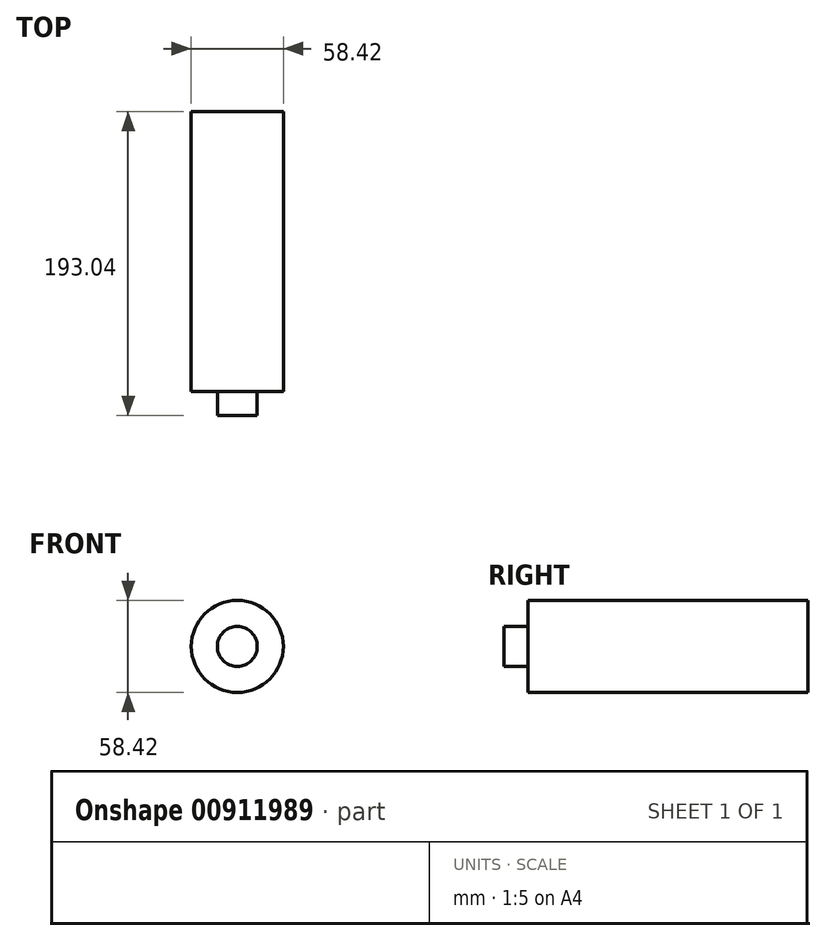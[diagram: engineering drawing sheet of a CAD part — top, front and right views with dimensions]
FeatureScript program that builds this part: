
annotation { "Feature Type Name" : "Feature", "Feature Type Description" : "" }
export const myFeature = defineFeature(function(context is Context, id is Id, definition is map)
    precondition{}
    {
        {
            var Q0;
            Q0=qCreatedBy(makeId("Front.planeOp"),FACE);
            var sketch = newSketch(context, id + "F0", { "sketchPlane" : qUnion([Q0])});
            skCircle(sketch, "E0", {"center": v(0, 0) * mm, "radius": 29.21 * mm});
            skPoint(sketch, "E1.orphan", {"position": v(0, 29.21) * mm});
            skSolve(sketch);
        }
        {
            var Q0;
            Q0=makeQuery(id+"F0.imprint","IMPRINT",FACE,{"disambiguationData":[TD([[makeQuery(id+"F0.imprint","IMPRINT",EDGE,{"derivedFrom":sQuery(id+"F0.wireOp",EDGE,"E0")}),1.0]])]});
            extrude(context, id + "F1", {"entities" : qUnion([Q0]), "depth" : 177.8 * mm, "offsetDistance" : 25.4 * mm});
        }
        {
            var Q0;
            Q0=makeQuery(id+"F1.opExtrude","CAP_FACE",FACE,{"disambiguationData":[OSD([sQuery(id+"F0.wireOp",EDGE,"E0")])],"isStart":false});
            var sketch = newSketch(context, id + "F2", { "sketchPlane" : qUnion([Q0])});
            skCircle(sketch, "E2", {"center": v(0, 0) * mm, "radius": 12.7 * mm});
            skSolve(sketch);
        }
        {
            var Q0;
            Q0=makeQuery(id+"F2.imprint","IMPRINT",FACE,{"disambiguationData":[TD([[makeQuery(id+"F2.imprint","IMPRINT",EDGE,{"derivedFrom":sQuery(id+"F2.wireOp",EDGE,"E2")}),1.0]])]});
            extrude(context, id + "F3", {"entities" : qUnion([Q0]), "operationType" : NewBodyOperationType.ADD, "depth" : 15.24 * mm, "offsetDistance" : 25.4 * mm});
        }
    });
